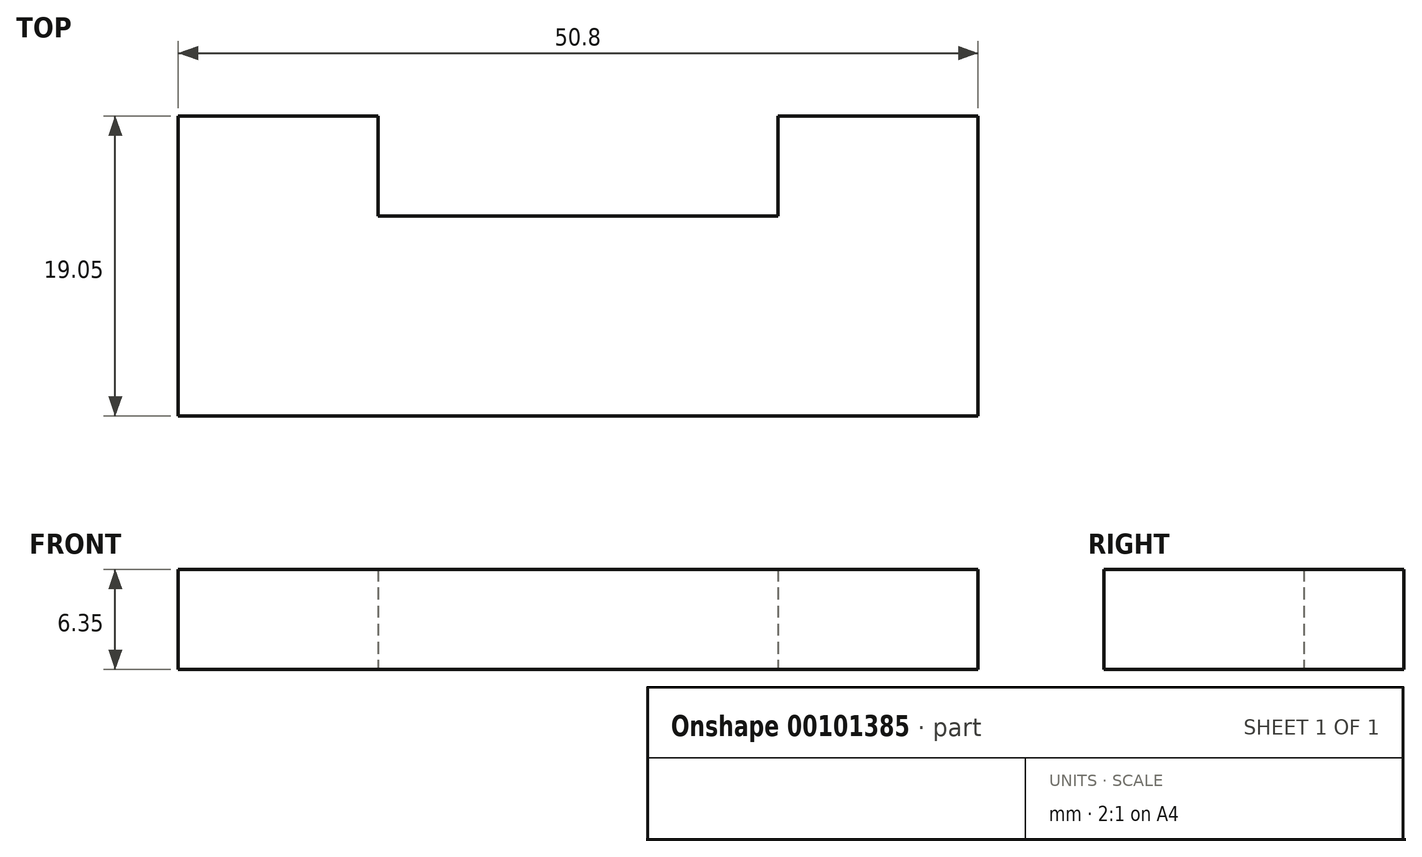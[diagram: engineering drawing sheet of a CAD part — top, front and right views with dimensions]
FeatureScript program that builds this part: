
annotation { "Feature Type Name" : "Feature", "Feature Type Description" : "" }
export const myFeature = defineFeature(function(context is Context, id is Id, definition is map)
    precondition{}
    {
        {
            var Q0;
            Q0=qCreatedBy(makeId("Top.planeOp"),FACE);
            var sketch = newSketch(context, id + "F0", { "sketchPlane" : qUnion([Q0])});
            skLineSegment(sketch, "E0.bottom", {"start": v(0, 0) * mm, "end": v(-50.8, 0) * mm});
            skLineSegment(sketch, "E0.top", {"start": v(0, 12.7) * mm, "end": v(-50.8, 12.7) * mm});
            skLineSegment(sketch, "E0.left", {"start": v(0, 0) * mm, "end": v(0, 12.7) * mm});
            skLineSegment(sketch, "E0.right", {"start": v(-50.8, 0) * mm, "end": v(-50.8, 12.7) * mm});
            skLineSegment(sketch, "E1.bottom", {"start": v(-50.8, 0) * mm, "end": v(-38.1, 0) * mm});
            skLineSegment(sketch, "E1.top", {"start": v(-50.8, -6.35) * mm, "end": v(-38.1, -6.35) * mm});
            skLineSegment(sketch, "E1.left", {"start": v(-50.8, 0) * mm, "end": v(-50.8, -6.35) * mm});
            skLineSegment(sketch, "E1.right", {"start": v(-38.1, 0) * mm, "end": v(-38.1, -6.35) * mm});
            skLineSegment(sketch, "E2.bottom", {"start": v(0, 0) * mm, "end": v(-12.7, 0) * mm});
            skLineSegment(sketch, "E2.top", {"start": v(0, -6.35) * mm, "end": v(-12.7, -6.35) * mm});
            skLineSegment(sketch, "E2.left", {"start": v(0, 0) * mm, "end": v(0, -6.35) * mm});
            skLineSegment(sketch, "E2.right", {"start": v(-12.7, 0) * mm, "end": v(-12.7, -6.35) * mm});
            skLineSegment(sketch, "E3.0.1.0", {"start": v(-38.1, 19.05) * mm, "end": v(-38.1, 12.7) * mm});
            skLineSegment(sketch, "E3.0.1.1", {"start": v(-50.8, 19.05) * mm, "end": v(-38.1, 19.05) * mm});
            skLineSegment(sketch, "E3.0.1.2", {"start": v(-50.8, 19.05) * mm, "end": v(-50.8, 12.7) * mm});
            skLineSegment(sketch, "E3.0.1.3", {"start": v(-50.8, 12.7) * mm, "end": v(-38.1, 12.7) * mm});
            skLineSegment(sketch, "E3.0.1.4", {"start": v(-12.7, 19.05) * mm, "end": v(-12.7, 12.7) * mm});
            skLineSegment(sketch, "E3.0.1.5", {"start": v(0, 19.05) * mm, "end": v(-12.7, 19.05) * mm});
            skLineSegment(sketch, "E3.0.1.6", {"start": v(0, 12.7) * mm, "end": v(-12.7, 12.7) * mm});
            skLineSegment(sketch, "E3.0.1.7", {"start": v(0, 19.05) * mm, "end": v(0, 12.7) * mm});
            skLineSegment(sketch, "E3.direction1", {"start": v(-38.1, -6.35) * mm, "end": v(-63.5, -6.35) * mm, "construction": true});
            skLineSegment(sketch, "E3.direction2", {"start": v(-38.1, -6.35) * mm, "end": v(-38.1, 12.7) * mm, "construction": true});
            skSolve(sketch);
        }
        {
            var Q0;
            Q0=makeQuery(id+"F0.imprint","IMPRINT",FACE,{"disambiguationData":[TD([[makeQuery(id+"F0.imprint","IMPRINT",EDGE,{"derivedFrom":sQuery(id+"F0.wireOp",EDGE,"E0.bottom")}),-1.0]])]});
            var Q1;
            Q1=makeQuery(id+"F0.imprint","IMPRINT",FACE,{"disambiguationData":[TD([[makeQuery(id+"F0.imprint","IMPRINT",EDGE,{"derivedFrom":sQuery(id+"F0.wireOp",EDGE,"E3.0.1.0")}),-1.0]])]});
            var Q2;
            Q2=makeQuery(id+"F0.imprint","IMPRINT",FACE,{"disambiguationData":[TD([[makeQuery(id+"F0.imprint","IMPRINT",EDGE,{"derivedFrom":sQuery(id+"F0.wireOp",EDGE,"E3.0.1.4")}),1.0]])]});
            var Q3;
            Q3=makeQuery(id+"F0.imprint","IMPRINT",FACE,{"disambiguationData":[TD([[makeQuery(id+"F0.imprint","IMPRINT",EDGE,{"derivedFrom":sQuery(id+"F0.wireOp",EDGE,"E2.bottom")}),1.0]])]});
            var Q4;
            Q4=makeQuery(id+"F0.imprint","IMPRINT",FACE,{"disambiguationData":[TD([[makeQuery(id+"F0.imprint","IMPRINT",EDGE,{"derivedFrom":sQuery(id+"F0.wireOp",EDGE,"E1.bottom")}),-1.0]])]});
            extrude(context, id + "F1", {"entities" : qUnion([Q0, Q1, Q2, Q3, Q4]), "depth" : 6.35 * mm});
        }
    });
